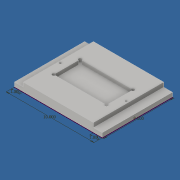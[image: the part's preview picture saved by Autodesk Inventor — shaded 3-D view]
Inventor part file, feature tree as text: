
AUTODESK INVENTOR PART (.ipt)
format: ipt  version: 2,016 (Build 200138000, 138)  size: 177,152 bytes
history: native  units: in
note: dims shown in document units (in); Inventor stores cm internally (conversion verified against a paired STEP export)
features: extrude x4, sketch x3, mirror x1
ambient origin geometry x8: Origin, YZ Plane, XZ Plane, XY Plane, X Axis, Y Axis, Z Axis, Center Point
bodies: Solid1 (feature_tree)
feature tree (8):
  sketch  "Sketch1"  dims[d0=10.0in d1=8.0in]
  extrude  "Extrusion1"  Depth=8.0in
  extrude  "Extrusion2"  Depth=1.0in
  extrude  "Extrusion3"  Depth=0.5in TaperAngle=0.0deg
  extrude  "Extrusion4"  Depth=6.0in
  mirror  "Mirror1"
  sketch  "Sketch2"  dims[d2=1.0in d3=1.0in]
  sketch  "Sketch3"  dims[d4=1.0in d5=0.0in d6=0.5in d7=0.0in d8=6.0in d9=3.0in d10=0.375in d11=0.375in d12=0.375in d13=0.375in d14=0.45in d15=0.0in d16=0.25in d17=0.75in d18=0.5in d19=0.0in]
